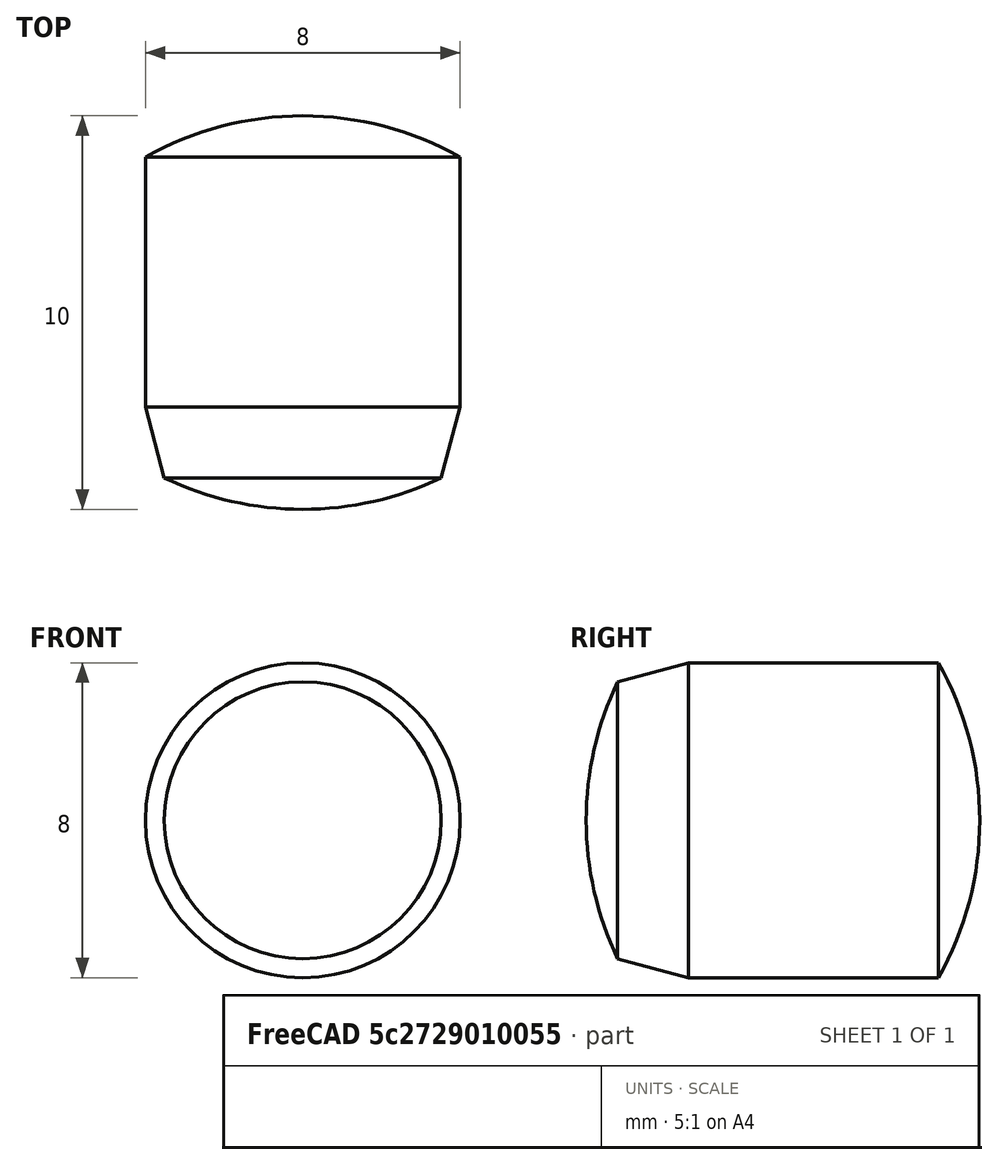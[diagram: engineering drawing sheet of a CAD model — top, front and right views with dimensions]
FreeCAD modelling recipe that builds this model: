
FCSTD DOCUMENT  (FreeCAD 0.15R4470 (Git))
Label: Zyl-Stift_DIN_6325-8x10
License: CC-BY 3.0
LicenseURL: http://creativecommons.org/licenses/by/3.0/
objects: Sketcher::SketchObject×1, PartDesign::Revolution×1
note: 3 computed .brp shape members not serialized (recipe doc carries the construction recipe); baked Part::Feature solids carry a one-line shape summary decoded from their .brp

FEATURE [Sketcher::SketchObject] Sketch
  Placement = pos=(0,0,0) rot=(0.57735,0.57735,0.57735;2.0944rad)
  sketch-geometry (5):
    g0: ArcOfCircle CenterX=7.33385 CenterY=0 CenterZ=0 NormalX=0 NormalY=0 NormalZ=1 Radius=8.13385 StartAngle=2.69436 EndAngle=3.14159
    g1: LineSegment StartX=0 StartY=3.51769 StartZ=0 EndX=1.8 EndY=4 EndZ=0
    g2: LineSegment StartX=1.8 StartY=4 StartZ=0 EndX=8.14849 EndY=4 EndZ=0
    g3: ArcOfCircle CenterX=1.06615 CenterY=0 CenterZ=0 NormalX=0 NormalY=0 NormalZ=1 Radius=8.13385 StartAngle=0 EndAngle=0.514124
    g4: LineSegment StartX=-0.8 StartY=0 StartZ=0 EndX=9.2 EndY=0 EndZ=0
  constraints (17):
    c: PointOnObject(g0,g-1)
    c: PointOnObject(g0,g-1)
    c: PointOnObject(g0,g-2)
    c: Coincident(g0,g1)
    c: Coincident(g1,g2)
    c: Horizontal(g2)
    c: PointOnObject(g3,g-1)
    c: Coincident(g3,g2)
    c: PointOnObject(g3,g-1)
    c: Coincident(g4,g0)
    c: Coincident(g4,g3)
    c: Equal(g0,g3)
    c: Angle(g4,g1) = 0.261799
    c: DistanceX(g4) = 10
    c: DistanceY(g-1,g1) = 4
    c: DistanceX(g1) = 1.8
    c: DistanceX(g0,g0) = 0.8
FEATURE [PartDesign::Revolution] Revolution  label="Zyl-Stift DIN 6325-8x10 #"
  Angle = 360
  Axis = (0,1,0)
  Base = (0,0,0)
  Placement = pos=(0,0,0) rot=(0.57735,0.57735,0.57735;2.0944rad)
  ReferenceAxis = -> Sketch [H_Axis]
  Sketch = -> Sketch
